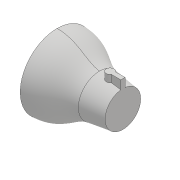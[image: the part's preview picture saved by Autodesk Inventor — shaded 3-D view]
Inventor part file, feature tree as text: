
AUTODESK INVENTOR PART (.ipt)
format: ipt  version: 2018 (Build 220112000, 112)  size: 164,864 bytes
history: native  units: mm
features: sketch x3, extrude x2, revolve x1, plane x1, projected_geometry x1
ambient origin geometry x8: Origin, YZ Plane, XZ Plane, XY Plane, X Axis, Y Axis, Z Axis, Center Point
bodies: Solid1 (feature_tree)
feature tree (8):
  revolve  "Revolution1"  [1 undecoded]
  plane  "Work Plane1"
  extrude  "Extrusion1"  Depth=45.0mm
  extrude  "Extrusion4"  Depth=10.0mm
  sketch  "Sketch1"  dims[d0=125.0mm d1=40.0mm]
  sketch  "Sketch2"  dims[d2=45.0mm d3=45.0mm]
  sketch  "Sketch6"  dims[d4=10.0mm d5=70.0mm d6=22.0mm d7=70.0mm d8=90.0deg d9=17.104227mm d14=50.0mm d15=15.0mm d16=38.0mm d17=10.0mm d18=0.0mm d39=20.0mm d40=10.0mm d41=0.0mm]
  projected_geometry  "Projected Loop3"
note: 1 required parameter value undecoded (feature->parameter linkage not recoverable at this tier; creation-order binding heuristic only, values carry confidence <= 0.55)
